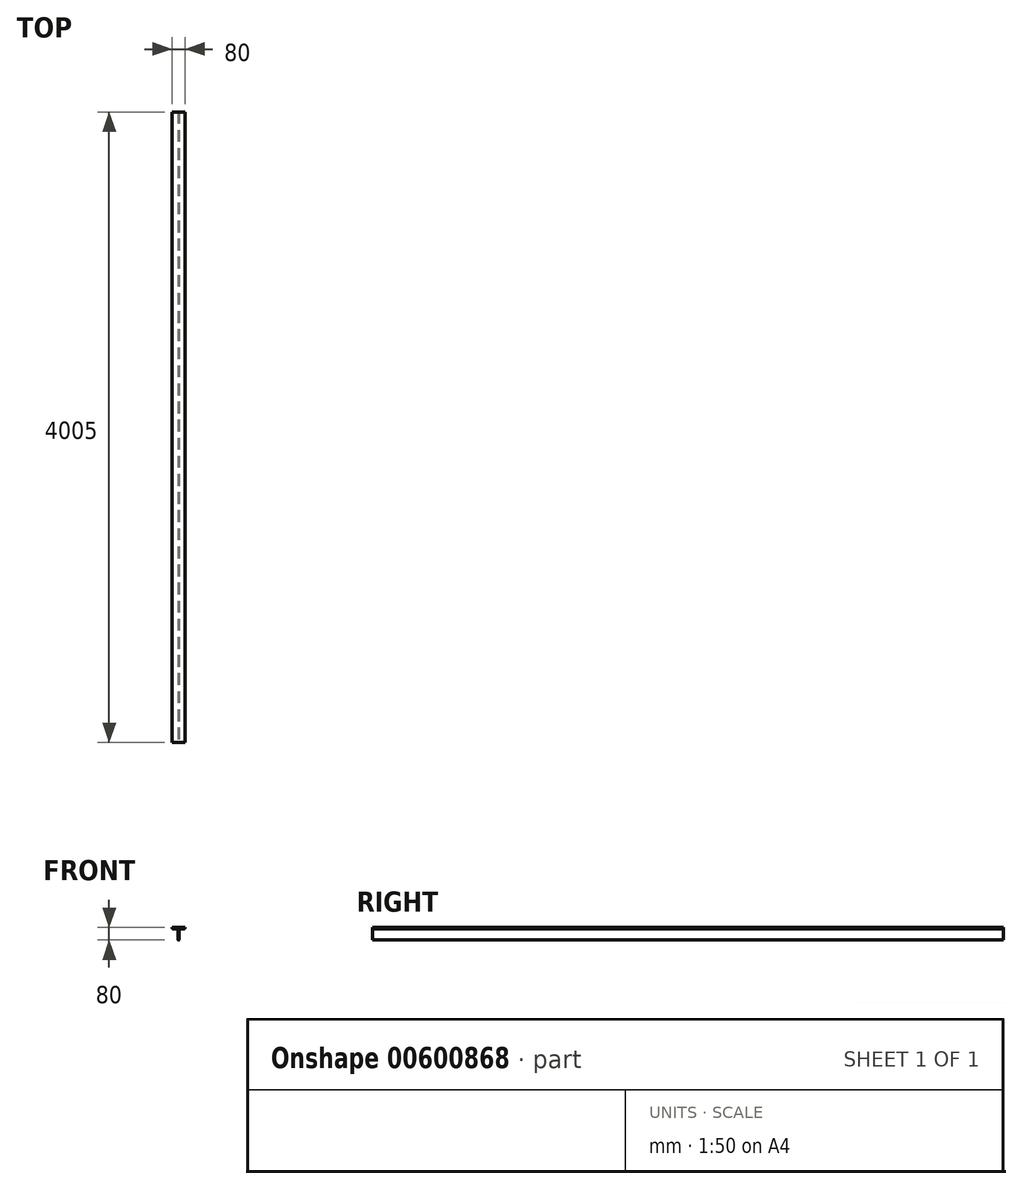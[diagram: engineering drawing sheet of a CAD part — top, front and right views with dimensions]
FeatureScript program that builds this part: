
annotation { "Feature Type Name" : "Feature", "Feature Type Description" : "" }
export const myFeature = defineFeature(function(context is Context, id is Id, definition is map)
    precondition{}
    {
        {
            var Q0;
            Q0=qCreatedBy(makeId("Front.planeOp"),FACE);
            var sketch = newSketch(context, id + "F0", { "sketchPlane" : qUnion([Q0])});
            skLineSegment(sketch, "E0.bottom", {"start": v(0, 0) * mm, "end": v(80, 0) * mm});
            skLineSegment(sketch, "E0.top", {"start": v(4.5, -9) * mm, "end": v(26.5, -9) * mm});
            skLineSegment(sketch, "E0.left", {"start": v(0, 0) * mm, "end": v(0, -4.5) * mm});
            skLineSegment(sketch, "E0.right", {"start": v(80, 0) * mm, "end": v(80, -4.5) * mm});
            skLineSegment(sketch, "E1.bottom", {"start": v(35.5, 0) * mm, "end": v(44.5, 0) * mm});
            skLineSegment(sketch, "E1.top", {"start": v(37.5, -80) * mm, "end": v(42.5, -80) * mm});
            skLineSegment(sketch, "E1.left", {"start": v(35.5, -18) * mm, "end": v(35.5, -78) * mm});
            skLineSegment(sketch, "E1.right", {"start": v(44.5, -18) * mm, "end": v(44.5, -78) * mm});
            skPoint(sketch, "E2.visualSharp", {"position": v(0, -9) * mm});
            skArc(sketch, "E2.filletArc", {"start": v(0, -4.5) * mm, "mid": v(1.32, -7.68) * mm, "end": v(4.5, -9) * mm});
            skPoint(sketch, "E3.visualSharp", {"position": v(80, -9) * mm});
            skArc(sketch, "E3.filletArc", {"start": v(75.5, -9) * mm, "mid": v(78.68, -7.68) * mm, "end": v(80, -4.5) * mm});
            skLineSegment(sketch, "E4.trimOffspring", {"start": v(53.5, -9) * mm, "end": v(75.5, -9) * mm});
            skPoint(sketch, "E5.visualSharp", {"position": v(44.5, -9) * mm});
            skArc(sketch, "E5.filletArc", {"start": v(53.5, -9) * mm, "mid": v(47.14, -11.64) * mm, "end": v(44.5, -18) * mm});
            skPoint(sketch, "E6.visualSharp", {"position": v(35.5, -9) * mm});
            skArc(sketch, "E6.filletArc", {"start": v(35.5, -18) * mm, "mid": v(32.86, -11.64) * mm, "end": v(26.5, -9) * mm});
            skPoint(sketch, "E7.visualSharp", {"position": v(35.5, -80) * mm});
            skArc(sketch, "E7.filletArc", {"start": v(35.5, -78) * mm, "mid": v(36.09, -79.41) * mm, "end": v(37.5, -80) * mm});
            skPoint(sketch, "E8.visualSharp", {"position": v(44.5, -80) * mm});
            skArc(sketch, "E8.filletArc", {"start": v(42.5, -80) * mm, "mid": v(43.91, -79.41) * mm, "end": v(44.5, -78) * mm});
            skSolve(sketch);
        }
        {
            var Q0;
            Q0=makeQuery(id+"F0.imprint","IMPRINT",FACE,{"disambiguationData":[TD([[makeQuery(id+"F0.imprint","IMPRINT",EDGE,{"derivedFrom":sQuery(id+"F0.wireOp",EDGE,"E0.top")}),1.0]])]});
            extrude(context, id + "F1", {"entities" : qUnion([Q0]), "oppositeDirection" : true, "depth" : 4005 * mm, "offsetDistance" : 25 * mm});
        }
    });
